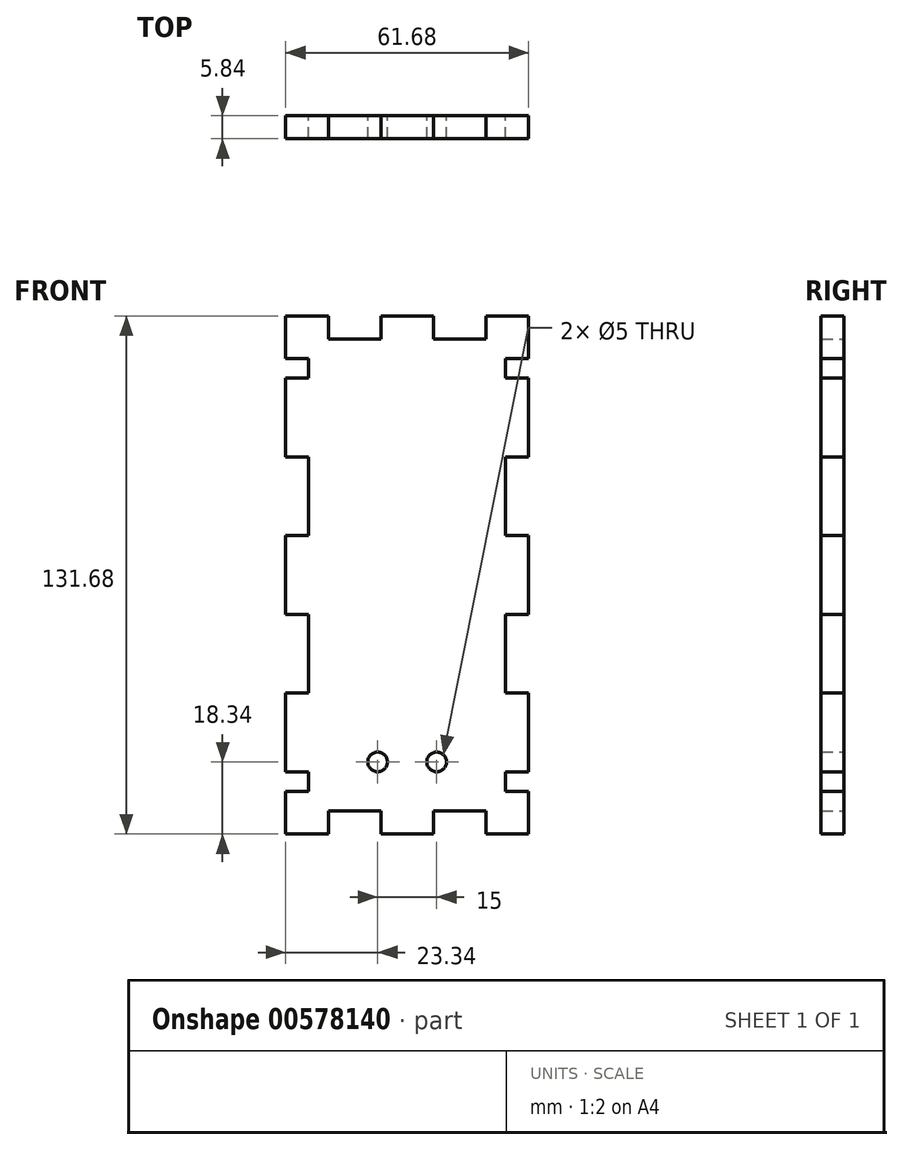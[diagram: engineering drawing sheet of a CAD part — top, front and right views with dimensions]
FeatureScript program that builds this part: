
annotation { "Feature Type Name" : "Feature", "Feature Type Description" : "" }
export const myFeature = defineFeature(function(context is Context, id is Id, definition is map)
    precondition{}
    {
        {
            var Q0;
            Q0=qCreatedBy(makeId("Front.planeOp"),FACE);
            var sketch = newSketch(context, id + "F0", { "sketchPlane" : qUnion([Q0])});
            skLineSegment(sketch, "E0.bottom", {"start": v(-25, 60) * mm, "end": v(25, 60) * mm});
            skLineSegment(sketch, "E0.top", {"start": v(-25, -60) * mm, "end": v(25, -60) * mm});
            skLineSegment(sketch, "E0.left", {"start": v(-25, 60) * mm, "end": v(-25, -60) * mm});
            skLineSegment(sketch, "E0.right", {"start": v(25, 60) * mm, "end": v(25, -60) * mm});
            skLineSegment(sketch, "E1.bottom", {"start": v(30.84, 65.84) * mm, "end": v(20, 65.84) * mm});
            skLineSegment(sketch, "E1.top", {"start": v(30.84, -65.84) * mm, "end": v(20, -65.84) * mm});
            skLineSegment(sketch, "E1.left", {"start": v(30.84, 65.84) * mm, "end": v(30.84, 55) * mm});
            skLineSegment(sketch, "E1.right", {"start": v(-30.84, 65.84) * mm, "end": v(-30.84, 55) * mm});
            skPoint(sketch, "E1.middle", {"position": v(0, 0) * mm});
            skLineSegment(sketch, "E2.bottom", {"start": v(6.67, -65.84) * mm, "end": v(-6.67, -65.84) * mm});
            skLineSegment(sketch, "E2.left", {"start": v(6.67, -65.84) * mm, "end": v(6.67, -60) * mm});
            skLineSegment(sketch, "E2.right", {"start": v(-6.67, -65.84) * mm, "end": v(-6.67, -60) * mm});
            skPoint(sketch, "E2.middle", {"position": v(0, -60) * mm});
            skPoint(sketch, "E3.middle", {"position": v(-25, -60) * mm});
            skLineSegment(sketch, "E4.bottom", {"start": v(-6.67, 65.84) * mm, "end": v(6.67, 65.84) * mm});
            skLineSegment(sketch, "E4.left", {"start": v(-6.67, 65.84) * mm, "end": v(-6.67, 60) * mm});
            skLineSegment(sketch, "E4.right", {"start": v(6.67, 65.84) * mm, "end": v(6.67, 60) * mm});
            skPoint(sketch, "E4.middle", {"position": v(0, 60) * mm});
            skPoint(sketch, "E5.middle", {"position": v(-25, 60) * mm});
            skPoint(sketch, "E6.middle", {"position": v(25, 60) * mm});
            skLineSegment(sketch, "E7.bottom", {"start": v(-6.67, 60) * mm, "end": v(-20, 60) * mm});
            skLineSegment(sketch, "E7.left", {"start": v(-6.67, 60) * mm, "end": v(-6.67, 65.84) * mm});
            skLineSegment(sketch, "E7.right", {"start": v(-20, 60) * mm, "end": v(-20, 65.84) * mm});
            skLineSegment(sketch, "E8.bottom", {"start": v(6.67, 60) * mm, "end": v(20, 60) * mm});
            skLineSegment(sketch, "E8.left", {"start": v(6.67, 60) * mm, "end": v(6.67, 65.84) * mm});
            skLineSegment(sketch, "E8.right", {"start": v(20, 60) * mm, "end": v(20, 65.84) * mm});
            skLineSegment(sketch, "E9.bottom", {"start": v(-6.67, -60) * mm, "end": v(-20, -60) * mm});
            skLineSegment(sketch, "E9.left", {"start": v(-6.67, -60) * mm, "end": v(-6.67, -65.84) * mm});
            skLineSegment(sketch, "E9.right", {"start": v(-20, -60) * mm, "end": v(-20, -65.84) * mm});
            skLineSegment(sketch, "E10.bottom", {"start": v(6.67, -60) * mm, "end": v(20, -60) * mm});
            skLineSegment(sketch, "E10.left", {"start": v(6.67, -60) * mm, "end": v(6.67, -65.84) * mm});
            skLineSegment(sketch, "E10.right", {"start": v(20, -60) * mm, "end": v(20, -65.84) * mm});
            skLineSegment(sketch, "E11.trimOffspring", {"start": v(-20, 65.84) * mm, "end": v(-30.84, 65.84) * mm});
            skLineSegment(sketch, "E12.trimOffspring", {"start": v(6.67, 65.84) * mm, "end": v(-6.67, 65.84) * mm});
            skPoint(sketch, "E13.orphan", {"position": v(-6.67, 54.16) * mm});
            skPoint(sketch, "E14.orphan", {"position": v(6.67, 54.16) * mm});
            skPoint(sketch, "E15.orphan", {"position": v(-6.67, -54.16) * mm});
            skPoint(sketch, "E16.orphan", {"position": v(6.67, -54.16) * mm});
            skLineSegment(sketch, "E17.trimOffspring", {"start": v(-20, -65.84) * mm, "end": v(-30.84, -65.84) * mm});
            skLineSegment(sketch, "E18.bottom", {"start": v(-25, 10) * mm, "end": v(-30.84, 10) * mm});
            skLineSegment(sketch, "E18.top", {"start": v(-25, -10) * mm, "end": v(-30.84, -10) * mm});
            skLineSegment(sketch, "E18.left", {"start": v(-25, 10) * mm, "end": v(-25, -10) * mm});
            skPoint(sketch, "E18.middle", {"position": v(-30.84, 0) * mm});
            skLineSegment(sketch, "E19.bottom", {"start": v(-30.84, 10) * mm, "end": v(-25, 10) * mm});
            skLineSegment(sketch, "E19.top", {"start": v(-30.84, 30) * mm, "end": v(-25, 30) * mm});
            skLineSegment(sketch, "E19.right", {"start": v(-25, 10) * mm, "end": v(-25, 30) * mm});
            skPoint(sketch, "E19.middle", {"position": v(-30.84, 20) * mm});
            skLineSegment(sketch, "E20.bottom", {"start": v(-30.84, -10) * mm, "end": v(-25, -10) * mm});
            skLineSegment(sketch, "E20.top", {"start": v(-30.84, -30) * mm, "end": v(-25, -30) * mm});
            skLineSegment(sketch, "E20.right", {"start": v(-25, -10) * mm, "end": v(-25, -30) * mm});
            skPoint(sketch, "E20.middle", {"position": v(-30.84, -20) * mm});
            skLineSegment(sketch, "E21.top", {"start": v(-30.84, 50) * mm, "end": v(-25, 50) * mm});
            skLineSegment(sketch, "E21.right", {"start": v(-25, 30) * mm, "end": v(-25, 50) * mm});
            skPoint(sketch, "E21.middle", {"position": v(-30.84, 40) * mm});
            skPoint(sketch, "E22.cornerSnap0", {"position": v(-36.68, 20) * mm});
            skLineSegment(sketch, "E23.top", {"start": v(-30.84, -50) * mm, "end": v(-25, -50) * mm});
            skLineSegment(sketch, "E23.right", {"start": v(-25, -30) * mm, "end": v(-25, -50) * mm});
            skPoint(sketch, "E23.middle", {"position": v(-30.84, -40) * mm});
            skLineSegment(sketch, "E24.top", {"start": v(-101.7, -103.63) * mm, "end": v(-97.86, -103.63) * mm});
            skLineSegment(sketch, "E25.bottom", {"start": v(-25, 55) * mm, "end": v(-30.84, 55) * mm});
            skLineSegment(sketch, "E25.top", {"start": v(-25, 50) * mm, "end": v(-30.84, 50) * mm});
            skLineSegment(sketch, "E25.left", {"start": v(-25, 55) * mm, "end": v(-25, 50) * mm});
            skLineSegment(sketch, "E26.bottom", {"start": v(-25, -50) * mm, "end": v(-30.84, -50) * mm});
            skLineSegment(sketch, "E26.top", {"start": v(-25, -55) * mm, "end": v(-30.84, -55) * mm});
            skLineSegment(sketch, "E26.left", {"start": v(-25, -50) * mm, "end": v(-25, -55) * mm});
            skLineSegment(sketch, "E27.bottom", {"start": v(25, 10) * mm, "end": v(30.84, 10) * mm});
            skLineSegment(sketch, "E27.top", {"start": v(25, -10) * mm, "end": v(30.84, -10) * mm});
            skLineSegment(sketch, "E27.left", {"start": v(25, 10) * mm, "end": v(25, -10) * mm});
            skPoint(sketch, "E27.middle", {"position": v(30.84, 0) * mm});
            skLineSegment(sketch, "E28.bottom", {"start": v(30.84, 10) * mm, "end": v(25, 10) * mm});
            skLineSegment(sketch, "E28.top", {"start": v(30.84, 30) * mm, "end": v(25, 30) * mm});
            skLineSegment(sketch, "E28.right", {"start": v(25, 10) * mm, "end": v(25, 30) * mm});
            skPoint(sketch, "E28.middle", {"position": v(30.84, 20) * mm});
            skLineSegment(sketch, "E29.bottom", {"start": v(30.84, -10) * mm, "end": v(25, -10) * mm});
            skLineSegment(sketch, "E29.top", {"start": v(30.84, -30) * mm, "end": v(25, -30) * mm});
            skLineSegment(sketch, "E29.right", {"start": v(25, -10) * mm, "end": v(25, -30) * mm});
            skPoint(sketch, "E29.middle", {"position": v(30.84, -20) * mm});
            skLineSegment(sketch, "E30.top", {"start": v(30.84, 50) * mm, "end": v(25, 50) * mm});
            skLineSegment(sketch, "E30.right", {"start": v(25, 30) * mm, "end": v(25, 50) * mm});
            skPoint(sketch, "E30.middle", {"position": v(30.84, 40) * mm});
            skLineSegment(sketch, "E31.top", {"start": v(30.84, -50) * mm, "end": v(25, -50) * mm});
            skLineSegment(sketch, "E31.right", {"start": v(25, -30) * mm, "end": v(25, -50) * mm});
            skPoint(sketch, "E31.middle", {"position": v(30.84, -40) * mm});
            skLineSegment(sketch, "E32.bottom", {"start": v(25, -50) * mm, "end": v(30.84, -50) * mm});
            skLineSegment(sketch, "E32.top", {"start": v(25, -55) * mm, "end": v(30.84, -55) * mm});
            skLineSegment(sketch, "E32.left", {"start": v(25, -50) * mm, "end": v(25, -55) * mm});
            skLineSegment(sketch, "E33.bottom", {"start": v(25, 55) * mm, "end": v(30.84, 55) * mm});
            skLineSegment(sketch, "E33.top", {"start": v(25, 50) * mm, "end": v(30.84, 50) * mm});
            skLineSegment(sketch, "E33.left", {"start": v(25, 55) * mm, "end": v(25, 50) * mm});
            skPoint(sketch, "E34.orphan", {"position": v(-36.68, 50) * mm});
            skPoint(sketch, "E35.orphan", {"position": v(-36.68, 30) * mm});
            skPoint(sketch, "E36.orphan", {"position": v(-36.68, 10) * mm});
            skPoint(sketch, "E37.orphan", {"position": v(-36.68, -10) * mm});
            skPoint(sketch, "E38.orphan", {"position": v(-36.68, -30) * mm});
            skPoint(sketch, "E26.right.end.orphan", {"position": v(-36.68, -55) * mm});
            skPoint(sketch, "E39.orphan", {"position": v(-36.68, -50) * mm});
            skPoint(sketch, "E40.orphan", {"position": v(36.68, 10) * mm});
            skPoint(sketch, "E41.orphan", {"position": v(36.68, -10) * mm});
            skPoint(sketch, "E42.orphan", {"position": v(36.68, -30) * mm});
            skPoint(sketch, "E43.orphan", {"position": v(36.68, -50) * mm});
            skPoint(sketch, "E44.orphan", {"position": v(36.68, -55) * mm});
            skPoint(sketch, "E45.orphan", {"position": v(36.68, 50) * mm});
            skPoint(sketch, "E46.orphan", {"position": v(36.68, 30) * mm});
            skLineSegment(sketch, "E47.bottom", {"start": v(-20, 60) * mm, "end": v(-6.67, 60) * mm});
            skLineSegment(sketch, "E48.trimOffspring", {"start": v(-30.84, 50) * mm, "end": v(-30.84, 30) * mm});
            skLineSegment(sketch, "E49.trimOffspring", {"start": v(30.84, 50) * mm, "end": v(30.84, 30) * mm});
            skLineSegment(sketch, "E50.trimOffspring", {"start": v(30.84, 10) * mm, "end": v(30.84, -10) * mm});
            skLineSegment(sketch, "E51.trimOffspring", {"start": v(30.84, -30) * mm, "end": v(30.84, -50) * mm});
            skLineSegment(sketch, "E52.trimOffspring", {"start": v(30.84, -55) * mm, "end": v(30.84, -65.84) * mm});
            skLineSegment(sketch, "E53.trimOffspring", {"start": v(-30.84, -55) * mm, "end": v(-30.84, -65.84) * mm});
            skLineSegment(sketch, "E54.trimOffspring", {"start": v(-30.84, -20) * mm, "end": v(-30.84, -50) * mm});
            skLineSegment(sketch, "E55.trimOffspring", {"start": v(-30.84, 10) * mm, "end": v(-30.84, -10) * mm});
            skCircle(sketch, "E56", {"center": v(7.5, -47.5) * mm, "radius": 2.5 * mm});
            skCircle(sketch, "E57", {"center": v(-7.5, -47.5) * mm, "radius": 2.5 * mm});
            skSolve(sketch);
        }
        {
            var Q0;
            Q0 = qSketchRegion(id + "F0", true);
            extrude(context, id + "F1", {"entities" : qUnion([Q0]), "depth" : 5.84 * mm, "offsetDistance" : 25 * mm});
        }
    });
